# Revit family: Sanitary_Showers_AXOR_36754XXX-AXOR-ShowerSelect-ID-Thermostat__
name_source: partatom
category: Plumbing Fixtures
units: mm (PartAtom-declared; Revit-internal decimal feet)

## family parameters
Cut with Voids When Loaded = No
Host = Face
OmniClass Number = 23.31.17.00
OmniClass Title = Showers
Part Type = Normal
Room Calculation Point = No
Round Connector Dimension = Use Diameter
Shared = No

## types (1)
- Default - please load Revit Family Type Catalog
    Default Elevation = 1219 mm
    Description = AXOR ShowerSelect ID Thermostat for concealed installation softsquare for 2 functions
    Manufacturer = Axor
    Material 1 = AXOR - Metal - 000 Chrome
    Material 2 = AXOR - Plastic - Black
    Model = 36754XXX
    Product Page URL = https://www.axor-design.com
    Product data url = https://bimobject.com
    URL = https://www.axor-design.com
    Version = 1

## geometry (parser evidence)
native form markers: Sweep x3
no freeform markers — native parametric forms only
